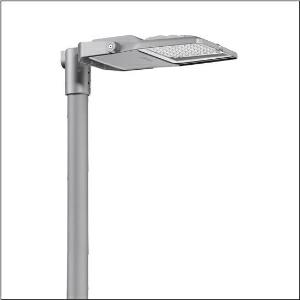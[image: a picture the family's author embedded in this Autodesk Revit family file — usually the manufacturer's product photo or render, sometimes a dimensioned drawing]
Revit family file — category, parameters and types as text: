
# Revit family: floodlight_fl_21_mini___pl33t_5xa7776c2f3a_ca81
name_source: partatom
category: Lighting Fixtures
units: mm (PartAtom-declared; Revit-internal decimal feet)

## family parameters
Cut with Voids When Loaded = No
Host = Face
Light Source = No
Part Type = Normal
Room Calculation Point = No
Round Connector Dimension = Use Diameter
Shared = No

## types (1)
- --- (1 x LED, 12050 lm, 89 W, 3000K)
    Apparent Load = 89 VA
    CIE Flux Codes = 26 75 99 100 100
    Color Rendering = 70
    Color Temperature = 3000K
    Default Elevation = 1800 mm
    Description = Floodlight FL 21 mini, floodlight, primary light control with lens, of PMMA, primary optical cover: protective disc, of toughened safety glass, transparent, light distribution: PL33T, light emission: direct distribution, installation type: surface-mounted, LED, High Power LED, rated luminous flux: 12.050lm, luminous efficacy: 135lm/W, light colour: 730, colour temperature: 3000K, control: flexible luminous flux parameterisation, time-dependent luminous flux control, constant luminous flux control, overheat protection, presetting dimming logarithmic, with terminal, 6-pole, mains connection: 220..240V, AC, 50/60Hz, start of lifetime: 89W, end of service life: 94W, reduction: 43W, luminaire housing, of diecast aluminium, powder-coated, Siteco® metallic grey (DB 702S), corrosivity category C5 mid according to DIN EN ISO 12944, sealing non-destructively replaceable, please order mast flange separately, mast bracket, of steel, galvanised, powder-coated, Siteco® metallic grey (DB 702S), Smart Interface below and above, protection rating (complete): IP66, insulation class (complete): insulation class II (safety insulation), certification: CE, ENEC, VDE, protection symbol: D, impact resistance: IK08, permissible operating ambient temperature: -40..+40°C, permissible operating ambient temperature for outdoor applications: -40..+50°C, standard: DIN EN 12944, LABS conformity tested according to VDMA 24364:2018-05, packaging unit: 1 piece

Light Distribution: PL33T
    Height = 70 mm
    Lamp = 1 x LED
    Lamp Light Flux = 12050 lm
    Lamp Power = 89 W
    Lamp count = 1
    Length = 485 mm
    Luminous efficacy = 135 lm/W
    Manufacturer = Siteco
    ModVariant = No
    Model = 5XA7776C2F3A
    Number of Poles = 1
    OnlyDefault = Yes
    Power Factor = 1
    Product Name = Floodlight FL 21 mini | PL33T
    Product group = floodlight | pylon annexe
    ProductGroupID = 6200
    Protection Class = Protection class II
    Protection Degree = IP 66
    RLX_Detail_Level = 1
    RLX_Emergency_Light_Flux = 0 lm
    RLX_Emergency_Type = 0
    RLX_Emergency_Type_DB = No
    RlxData = <blob elided: 100785 chars, md5=2efd8ada>
    Socket = socket
    Standby Power = 0 W
    System Light Flux = 12050 lm
    System Power = 89 W
    Type Comments = factory setting: luminous flux: 100 % | dim-lin: 254 | 456 mA
    Type Image = l_1007125.jpg
    URL = http://relux.com
    VarID = @adj_098635
    Voltage = 0 V
    Weight = 0.00 kg
    Width = 337 mm

## geometry (parser evidence)
native form markers: Blend x4, Sweep x12
no freeform markers — native parametric forms only
